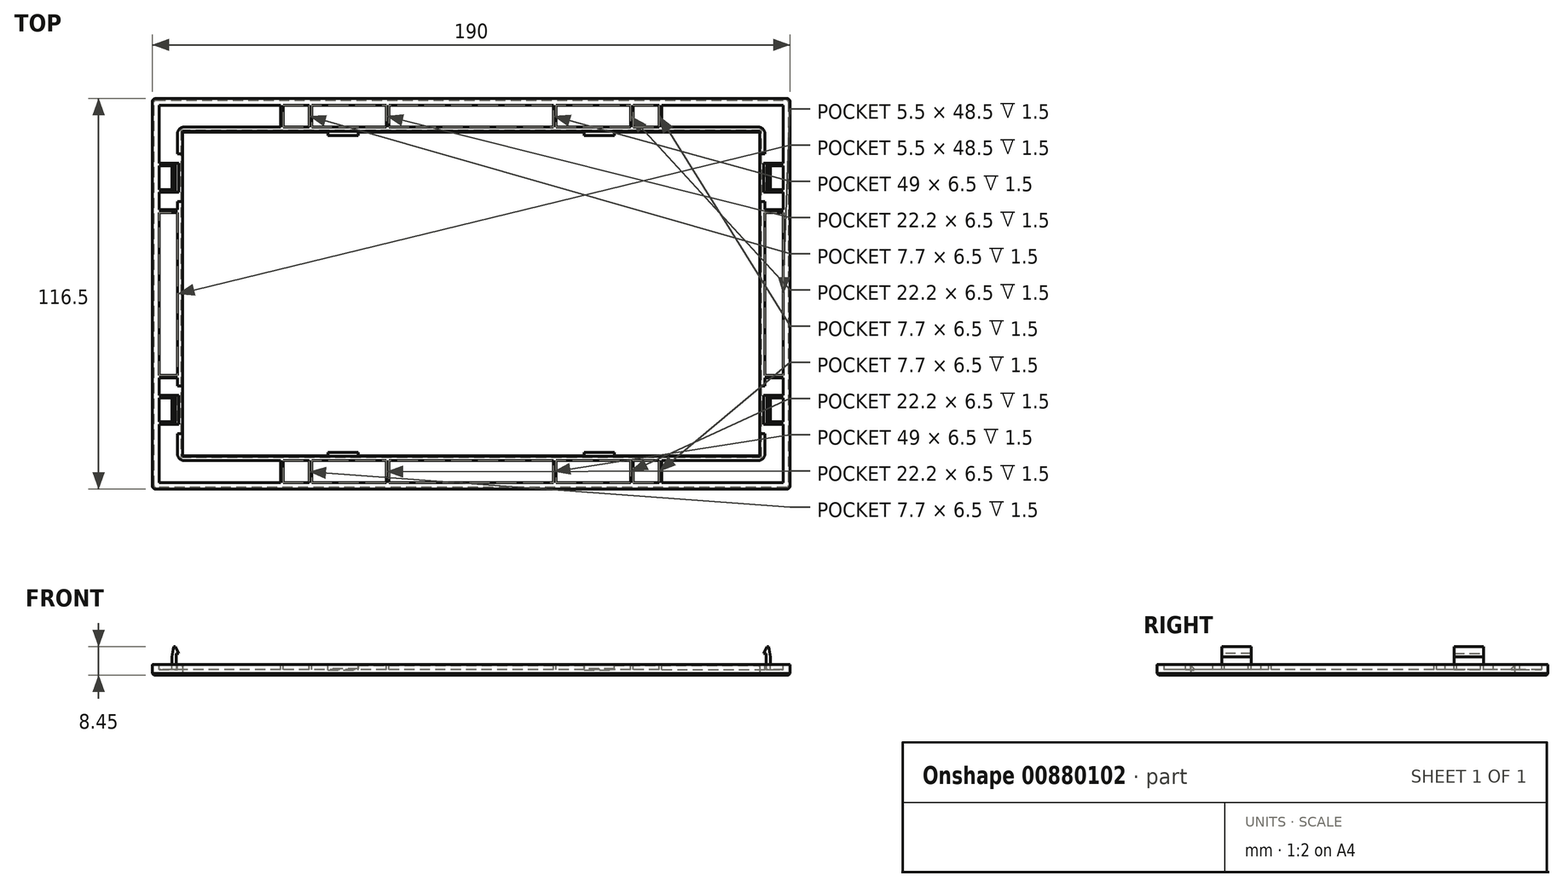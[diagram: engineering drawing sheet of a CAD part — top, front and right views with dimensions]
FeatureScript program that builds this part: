
annotation { "Feature Type Name" : "Feature", "Feature Type Description" : "" }
export const myFeature = defineFeature(function(context is Context, id is Id, definition is map)
    precondition{}
    {
        {
            var Q0;
            Q0=qCreatedBy(makeId("Top.planeOp"),FACE);
            var sketch = newSketch(context, id + "F0", { "sketchPlane" : qUnion([Q0])});
            skLineSegment(sketch, "E0", {"start": v(0, -58.25) * mm, "end": v(95, -58.25) * mm});
            skLineSegment(sketch, "E1", {"start": v(95, -58.25) * mm, "end": v(95, 0) * mm});
            skLineSegment(sketch, "E2", {"start": v(0, -48.25) * mm, "end": v(86, -48.25) * mm});
            skLineSegment(sketch, "E3", {"start": v(86, -48.25) * mm, "end": v(86, 0) * mm});
            skLineSegment(sketch, "E4.MirrorCS", {"start": v(95, 58.25) * mm, "end": v(95, 0) * mm});
            skLineSegment(sketch, "E5.MirrorCS", {"start": v(86, 48.25) * mm, "end": v(86, 0) * mm});
            skLineSegment(sketch, "E6.MirrorCS", {"start": v(0, 48.25) * mm, "end": v(86, 48.25) * mm});
            skLineSegment(sketch, "E7.MirrorCS", {"start": v(0, 58.25) * mm, "end": v(95, 58.25) * mm});
            skLineSegment(sketch, "E8.MirrorCS", {"start": v(0, 58.25) * mm, "end": v(-95, 58.25) * mm});
            skLineSegment(sketch, "E9.MirrorCS", {"start": v(0, 48.25) * mm, "end": v(-86, 48.25) * mm});
            skLineSegment(sketch, "E10.MirrorCS", {"start": v(-86, 48.25) * mm, "end": v(-86, 0) * mm});
            skLineSegment(sketch, "E11.MirrorCS", {"start": v(-95, 58.25) * mm, "end": v(-95, 0) * mm});
            skLineSegment(sketch, "E12.MirrorCS", {"start": v(-95, -58.25) * mm, "end": v(-95, 0) * mm});
            skLineSegment(sketch, "E13.MirrorCS", {"start": v(-86, -48.25) * mm, "end": v(-86, 0) * mm});
            skLineSegment(sketch, "E14.MirrorCS", {"start": v(0, -58.25) * mm, "end": v(-95, -58.25) * mm});
            skLineSegment(sketch, "E15.MirrorCS", {"start": v(0, -48.25) * mm, "end": v(-86, -48.25) * mm});
            skSolve(sketch);
        }
        {
            var Q0;
            Q0=makeQuery(id+"F0.imprint","IMPRINT",FACE,{"disambiguationData":[TD([[makeQuery(id+"F0.imprint","IMPRINT",EDGE,{"derivedFrom":sQuery(id+"F0.wireOp",EDGE,"E0")}),1.0]])]});
            extrude(context, id + "F1", {"entities" : qUnion([Q0]), "depth" : 1.65 * mm, "offsetDistance" : 25 * mm});
        }
        {
            var Q0;
            Q0=makeQuery(id+"F1.opExtrude","CAP_FACE",FACE,{"disambiguationData":[OSD([sQuery(id+"F0.wireOp",EDGE,"E0"),sQuery(id+"F0.wireOp",EDGE,"E1"),sQuery(id+"F0.wireOp",EDGE,"E2"),sQuery(id+"F0.wireOp",EDGE,"E3"),sQuery(id+"F0.wireOp",EDGE,"E4.MirrorCS"),sQuery(id+"F0.wireOp",EDGE,"E5.MirrorCS"),sQuery(id+"F0.wireOp",EDGE,"E6.MirrorCS"),sQuery(id+"F0.wireOp",EDGE,"E7.MirrorCS"),sQuery(id+"F0.wireOp",EDGE,"E8.MirrorCS"),sQuery(id+"F0.wireOp",EDGE,"E9.MirrorCS"),sQuery(id+"F0.wireOp",EDGE,"E10.MirrorCS"),sQuery(id+"F0.wireOp",EDGE,"E11.MirrorCS"),sQuery(id+"F0.wireOp",EDGE,"E12.MirrorCS"),sQuery(id+"F0.wireOp",EDGE,"E13.MirrorCS"),sQuery(id+"F0.wireOp",EDGE,"E14.MirrorCS"),sQuery(id+"F0.wireOp",EDGE,"E15.MirrorCS")])],"isStart":false});
            var sketch = newSketch(context, id + "F2", { "sketchPlane" : qUnion([Q0])});
            skLineSegment(sketch, "E16.0", {"start": v(0, 58.25) * mm, "end": v(-95, 58.25) * mm});
            skLineSegment(sketch, "E17.0", {"start": v(-95, 58.25) * mm, "end": v(-95, 0) * mm});
            skLineSegment(sketch, "E18.0", {"start": v(-95, -58.25) * mm, "end": v(-95, 0) * mm});
            skLineSegment(sketch, "E19.0", {"start": v(0, -58.25) * mm, "end": v(-95, -58.25) * mm});
            skLineSegment(sketch, "E20.0", {"start": v(0, -58.25) * mm, "end": v(95, -58.25) * mm});
            skLineSegment(sketch, "E21.0", {"start": v(95, -58.25) * mm, "end": v(95, 0) * mm});
            skLineSegment(sketch, "E22.0", {"start": v(95, 58.25) * mm, "end": v(95, 0) * mm});
            skLineSegment(sketch, "E23.0", {"start": v(0, 58.25) * mm, "end": v(95, 58.25) * mm});
            skLineSegment(sketch, "E24.0", {"start": v(0, 56.25) * mm, "end": v(93, 56.25) * mm});
            skLineSegment(sketch, "E24.1", {"start": v(93, 56.25) * mm, "end": v(93, 0) * mm});
            skLineSegment(sketch, "E24.2", {"start": v(0, 56.25) * mm, "end": v(-93, 56.25) * mm});
            skLineSegment(sketch, "E24.3", {"start": v(93, -56.25) * mm, "end": v(93, 0) * mm});
            skLineSegment(sketch, "E24.4", {"start": v(-93, 56.25) * mm, "end": v(-93, 0) * mm});
            skLineSegment(sketch, "E24.5", {"start": v(-93, -56.25) * mm, "end": v(-93, 0) * mm});
            skLineSegment(sketch, "E24.6", {"start": v(0, -56.25) * mm, "end": v(-93, -56.25) * mm});
            skLineSegment(sketch, "E24.7", {"start": v(0, -56.25) * mm, "end": v(93, -56.25) * mm});
            skSolve(sketch);
        }
        {
            var Q0;
            Q0 = qSketchRegion(id + "F2", true);
            extrude(context, id + "F3", {"entities" : qUnion([Q0]), "operationType" : NewBodyOperationType.ADD, "depth" : 1.5 * mm, "offsetDistance" : 25 * mm});
        }
        {
            var Q0;
            Q0=makeQuery(id+"F3.boolean.opBoolean","MERGE",EDGE,{"derivedFrom":[makeQuery(id+"F1.opExtrude","SWEPT_EDGE",EDGE,{"disambiguationData":[OSD([sQuery(id+"F0.wireOp",EDGE,"E12.MirrorCS"),sQuery(id+"F0.wireOp",EDGE,"E14.MirrorCS")])]}),makeQuery(id+"F3.opExtrude","SWEPT_EDGE",EDGE,{"disambiguationData":[OSD([sQuery(id+"F2.wireOp",EDGE,"E18.0"),sQuery(id+"F2.wireOp",EDGE,"E19.0")])]})]});
            var Q1;
            Q1=makeQuery(id+"F3.boolean.opBoolean","MERGE",EDGE,{"derivedFrom":[makeQuery(id+"F1.opExtrude","SWEPT_EDGE",EDGE,{"disambiguationData":[OSD([sQuery(id+"F0.wireOp",EDGE,"E0"),sQuery(id+"F0.wireOp",EDGE,"E1")])]}),makeQuery(id+"F3.opExtrude","SWEPT_EDGE",EDGE,{"disambiguationData":[OSD([sQuery(id+"F2.wireOp",EDGE,"E20.0"),sQuery(id+"F2.wireOp",EDGE,"E21.0")])]})]});
            var Q2;
            Q2=makeQuery(id+"F3.boolean.opBoolean","MERGE",EDGE,{"derivedFrom":[makeQuery(id+"F1.opExtrude","SWEPT_EDGE",EDGE,{"disambiguationData":[OSD([sQuery(id+"F0.wireOp",EDGE,"E4.MirrorCS"),sQuery(id+"F0.wireOp",EDGE,"E7.MirrorCS")])]}),makeQuery(id+"F3.opExtrude","SWEPT_EDGE",EDGE,{"disambiguationData":[OSD([sQuery(id+"F2.wireOp",EDGE,"E22.0"),sQuery(id+"F2.wireOp",EDGE,"E23.0")])]})]});
            var Q3;
            Q3=makeQuery(id+"F3.boolean.opBoolean","MERGE",EDGE,{"derivedFrom":[makeQuery(id+"F1.opExtrude","SWEPT_EDGE",EDGE,{"disambiguationData":[OSD([sQuery(id+"F0.wireOp",EDGE,"E8.MirrorCS"),sQuery(id+"F0.wireOp",EDGE,"E11.MirrorCS")])]}),makeQuery(id+"F3.opExtrude","SWEPT_EDGE",EDGE,{"disambiguationData":[OSD([sQuery(id+"F2.wireOp",EDGE,"E16.0"),sQuery(id+"F2.wireOp",EDGE,"E17.0")])]})]});
            fillet(context, id + "F4", {"entities" : qUnion([Q0, Q1, Q2, Q3]), "radius" : 1 * mm, "tangentPropagation" : true, "allowEdgeOverflow" : false});
        }
        {
            var Q0;
            Q0=makeQuery(id+"F1.opExtrude","CAP_EDGE",EDGE,{"disambiguationData":[OSD([sQuery(id+"F0.wireOp",EDGE,"E1"),sQuery(id+"F0.wireOp",EDGE,"E4.MirrorCS")])],"isStart":true});
            var Q1;
            Q1=makeQuery(id+"F1.opExtrude","CAP_EDGE",EDGE,{"disambiguationData":[OSD([sQuery(id+"F0.wireOp",EDGE,"E7.MirrorCS"),sQuery(id+"F0.wireOp",EDGE,"E8.MirrorCS")])],"isStart":true});
            var Q2;
            Q2=makeQuery(id+"F1.opExtrude","CAP_EDGE",EDGE,{"disambiguationData":[OSD([sQuery(id+"F0.wireOp",EDGE,"E11.MirrorCS"),sQuery(id+"F0.wireOp",EDGE,"E12.MirrorCS")])],"isStart":true});
            var Q3;
            Q3=makeQuery(id+"F1.opExtrude","CAP_EDGE",EDGE,{"disambiguationData":[OSD([sQuery(id+"F0.wireOp",EDGE,"E0"),sQuery(id+"F0.wireOp",EDGE,"E14.MirrorCS")])],"isStart":true});
            var Q4;
            Q4=makeQuery(id+"F1.opExtrude","CAP_EDGE",EDGE,{"disambiguationData":[OSD([sQuery(id+"F0.wireOp",EDGE,"E3"),sQuery(id+"F0.wireOp",EDGE,"E5.MirrorCS")])],"isStart":true});
            var Q5;
            Q5=makeQuery(id+"F1.opExtrude","CAP_EDGE",EDGE,{"disambiguationData":[OSD([sQuery(id+"F0.wireOp",EDGE,"E6.MirrorCS"),sQuery(id+"F0.wireOp",EDGE,"E9.MirrorCS")])],"isStart":true});
            var Q6;
            Q6=makeQuery(id+"F1.opExtrude","CAP_EDGE",EDGE,{"disambiguationData":[OSD([sQuery(id+"F0.wireOp",EDGE,"E10.MirrorCS"),sQuery(id+"F0.wireOp",EDGE,"E13.MirrorCS")])],"isStart":true});
            var Q7;
            Q7=makeQuery(id+"F1.opExtrude","CAP_EDGE",EDGE,{"disambiguationData":[OSD([sQuery(id+"F0.wireOp",EDGE,"E2"),sQuery(id+"F0.wireOp",EDGE,"E15.MirrorCS")])],"isStart":true});
            chamfer(context, id + "F5", {"entities" : qUnion([Q0, Q1, Q2, Q3, Q4, Q5, Q6, Q7]), "width" : .5 * mm, "tangentPropagation" : true});
        }
        {
            var Q0;
            Q0=makeQuery(id+"F1.opExtrude","CAP_FACE",FACE,{"disambiguationData":[OSD([sQuery(id+"F0.wireOp",EDGE,"E0"),sQuery(id+"F0.wireOp",EDGE,"E1"),sQuery(id+"F0.wireOp",EDGE,"E2"),sQuery(id+"F0.wireOp",EDGE,"E3"),sQuery(id+"F0.wireOp",EDGE,"E4.MirrorCS"),sQuery(id+"F0.wireOp",EDGE,"E5.MirrorCS"),sQuery(id+"F0.wireOp",EDGE,"E6.MirrorCS"),sQuery(id+"F0.wireOp",EDGE,"E7.MirrorCS"),sQuery(id+"F0.wireOp",EDGE,"E8.MirrorCS"),sQuery(id+"F0.wireOp",EDGE,"E9.MirrorCS"),sQuery(id+"F0.wireOp",EDGE,"E10.MirrorCS"),sQuery(id+"F0.wireOp",EDGE,"E11.MirrorCS"),sQuery(id+"F0.wireOp",EDGE,"E12.MirrorCS"),sQuery(id+"F0.wireOp",EDGE,"E13.MirrorCS"),sQuery(id+"F0.wireOp",EDGE,"E14.MirrorCS"),sQuery(id+"F0.wireOp",EDGE,"E15.MirrorCS")])],"isStart":false});
            var sketch = newSketch(context, id + "F6", { "sketchPlane" : qUnion([Q0])});
            skLineSegment(sketch, "E25.0", {"start": v(-86, -48.25) * mm, "end": v(-86, 48.25) * mm});
            skLineSegment(sketch, "E26.0", {"start": v(86, 48.25) * mm, "end": v(-86, 48.25) * mm});
            skLineSegment(sketch, "E27.0", {"start": v(-86, -48.25) * mm, "end": v(86, -48.25) * mm});
            skLineSegment(sketch, "E28.0", {"start": v(86, 48.25) * mm, "end": v(86, -48.25) * mm});
            skLineSegment(sketch, "E29.0", {"start": v(87.5, 49.75) * mm, "end": v(-87.5, 49.75) * mm});
            skLineSegment(sketch, "E29.1", {"start": v(87.5, 49.75) * mm, "end": v(87.5, -49.75) * mm});
            skLineSegment(sketch, "E29.2", {"start": v(-87.5, -49.75) * mm, "end": v(87.5, -49.75) * mm});
            skLineSegment(sketch, "E29.3", {"start": v(-87.5, -49.75) * mm, "end": v(-87.5, 49.75) * mm});
            skPoint(sketch, "E30", {"position": v(-86, -41.75) * mm});
            skLineSegment(sketch, "E31", {"start": v(-86, -41.75) * mm, "end": v(-87.5, -41.75) * mm});
            skPoint(sketch, "E32", {"position": v(-86, -27.45) * mm});
            skLineSegment(sketch, "E33", {"start": v(-86, -27.45) * mm, "end": v(-87.5, -27.45) * mm});
            skLineSegment(sketch, "E34.MirrorCS", {"start": v(-86, 27.45) * mm, "end": v(-87.5, 27.45) * mm});
            skLineSegment(sketch, "E35.MirrorCS", {"start": v(-86, 41.75) * mm, "end": v(-87.5, 41.75) * mm});
            skLineSegment(sketch, "E36.MirrorCS", {"start": v(86, 41.75) * mm, "end": v(87.5, 41.75) * mm});
            skLineSegment(sketch, "E37.MirrorCS", {"start": v(86, 27.45) * mm, "end": v(87.5, 27.45) * mm});
            skLineSegment(sketch, "E38.MirrorCS", {"start": v(86, -27.45) * mm, "end": v(87.5, -27.45) * mm});
            skLineSegment(sketch, "E39.MirrorCS", {"start": v(86, -41.75) * mm, "end": v(87.5, -41.75) * mm});
            skSolve(sketch);
        }
        {
            var Q0;
            {var subQ4=sQuery(id+"F6.wireOp",EDGE,"E26.0");Q0=makeQuery(id+"F6.imprint","IMPRINT",FACE,{"disambiguationData":[TD([[makeQuery(id+"F6.imprint","IMPRINT",EDGE,{"derivedFrom":subQ4}),-1.0]])]});}
            var Q1;
            {var subQ0=sQuery(id+"F6.wireOp",EDGE,"E33");Q1=makeQuery(id+"F6.imprint","IMPRINT",FACE,{"disambiguationData":[TD([[makeQuery(id+"F6.imprint","IMPRINT",EDGE,{"derivedFrom":subQ0}),-1.0]])]});}
            var Q2;
            {var subQ3=sQuery(id+"F6.wireOp",EDGE,"E27.0");Q2=makeQuery(id+"F6.imprint","IMPRINT",FACE,{"disambiguationData":[TD([[makeQuery(id+"F6.imprint","IMPRINT",EDGE,{"derivedFrom":subQ3}),-1.0]])]});}
            var Q3;
            {var subQ0=sQuery(id+"F6.wireOp",EDGE,"E37.MirrorCS");Q3=makeQuery(id+"F6.imprint","IMPRINT",FACE,{"disambiguationData":[TD([[makeQuery(id+"F6.imprint","IMPRINT",EDGE,{"derivedFrom":subQ0}),-1.0]])]});}
            extrude(context, id + "F7", {"entities" : qUnion([Q0, Q1, Q2, Q3]), "operationType" : NewBodyOperationType.ADD, "depth" : 1.5 * mm, "offsetDistance" : 25 * mm});
        }
        {
            var Q0;
            Q0=makeQuery(id+"F7.opExtrude","SWEPT_EDGE",EDGE,{"disambiguationData":[OSD([sQuery(id+"F6.wireOp",EDGE,"E29.0"),sQuery(id+"F6.wireOp",EDGE,"E29.3")])]});
            var Q1;
            Q1=makeQuery(id+"F7.opExtrude","SWEPT_EDGE",EDGE,{"disambiguationData":[OSD([sQuery(id+"F6.wireOp",EDGE,"E29.2"),sQuery(id+"F6.wireOp",EDGE,"E29.3")])]});
            var Q2;
            Q2=makeQuery(id+"F7.opExtrude","SWEPT_EDGE",EDGE,{"disambiguationData":[OSD([sQuery(id+"F6.wireOp",EDGE,"E29.1"),sQuery(id+"F6.wireOp",EDGE,"E29.2")])]});
            var Q3;
            Q3=makeQuery(id+"F7.opExtrude","SWEPT_EDGE",EDGE,{"disambiguationData":[OSD([sQuery(id+"F6.wireOp",EDGE,"E29.0"),sQuery(id+"F6.wireOp",EDGE,"E29.1")])]});
            fillet(context, id + "F8", {"entities" : qUnion([Q0, Q1, Q2, Q3]), "radius" : 2 * mm, "tangentPropagation" : true, "allowEdgeOverflow" : false});
        }
        {
            var Q0;
            Q0=makeQuery(id+"F7.boolean.opBoolean","MERGE",EDGE,{"derivedFrom":[makeQuery(id+"F1.opExtrude","SWEPT_EDGE",EDGE,{"disambiguationData":[OSD([sQuery(id+"F0.wireOp",EDGE,"E9.MirrorCS"),sQuery(id+"F0.wireOp",EDGE,"E10.MirrorCS")])]}),makeQuery(id+"F7.opExtrude","SWEPT_EDGE",EDGE,{"disambiguationData":[OSD([sQuery(id+"F6.wireOp",EDGE,"E25.0"),sQuery(id+"F6.wireOp",EDGE,"E26.0")])]})]});
            var Q1;
            Q1=makeQuery(id+"F7.boolean.opBoolean","MERGE",EDGE,{"derivedFrom":[makeQuery(id+"F1.opExtrude","SWEPT_EDGE",EDGE,{"disambiguationData":[OSD([sQuery(id+"F0.wireOp",EDGE,"E13.MirrorCS"),sQuery(id+"F0.wireOp",EDGE,"E15.MirrorCS")])]}),makeQuery(id+"F7.opExtrude","SWEPT_EDGE",EDGE,{"disambiguationData":[OSD([sQuery(id+"F6.wireOp",EDGE,"E25.0"),sQuery(id+"F6.wireOp",EDGE,"E27.0")])]})]});
            var Q2;
            Q2=makeQuery(id+"F7.boolean.opBoolean","MERGE",EDGE,{"derivedFrom":[makeQuery(id+"F1.opExtrude","SWEPT_EDGE",EDGE,{"disambiguationData":[OSD([sQuery(id+"F0.wireOp",EDGE,"E2"),sQuery(id+"F0.wireOp",EDGE,"E3")])]}),makeQuery(id+"F7.opExtrude","SWEPT_EDGE",EDGE,{"disambiguationData":[OSD([sQuery(id+"F6.wireOp",EDGE,"E27.0"),sQuery(id+"F6.wireOp",EDGE,"E28.0")])]})]});
            var Q3;
            Q3=makeQuery(id+"F7.boolean.opBoolean","MERGE",EDGE,{"derivedFrom":[makeQuery(id+"F1.opExtrude","SWEPT_EDGE",EDGE,{"disambiguationData":[OSD([sQuery(id+"F0.wireOp",EDGE,"E5.MirrorCS"),sQuery(id+"F0.wireOp",EDGE,"E6.MirrorCS")])]}),makeQuery(id+"F7.opExtrude","SWEPT_EDGE",EDGE,{"disambiguationData":[OSD([sQuery(id+"F6.wireOp",EDGE,"E26.0"),sQuery(id+"F6.wireOp",EDGE,"E28.0")])]})]});
            fillet(context, id + "F9", {"entities" : qUnion([Q0, Q1, Q2, Q3]), "radius" : .5 * mm, "tangentPropagation" : true, "allowEdgeOverflow" : false});
        }
        {
            var Q0;
            Q0=makeQuery(id+"F3.opExtrude","CAP_FACE",FACE,{"disambiguationData":[OSD([sQuery(id+"F2.wireOp",EDGE,"E16.0"),sQuery(id+"F2.wireOp",EDGE,"E17.0"),sQuery(id+"F2.wireOp",EDGE,"E18.0"),sQuery(id+"F2.wireOp",EDGE,"E19.0"),sQuery(id+"F2.wireOp",EDGE,"E20.0"),sQuery(id+"F2.wireOp",EDGE,"E21.0"),sQuery(id+"F2.wireOp",EDGE,"E22.0"),sQuery(id+"F2.wireOp",EDGE,"E23.0"),sQuery(id+"F2.wireOp",EDGE,"E24.0"),sQuery(id+"F2.wireOp",EDGE,"E24.1"),sQuery(id+"F2.wireOp",EDGE,"E24.2"),sQuery(id+"F2.wireOp",EDGE,"E24.3"),sQuery(id+"F2.wireOp",EDGE,"E24.4"),sQuery(id+"F2.wireOp",EDGE,"E24.5"),sQuery(id+"F2.wireOp",EDGE,"E24.6"),sQuery(id+"F2.wireOp",EDGE,"E24.7")])],"isStart":false});
            var sketch = newSketch(context, id + "F10", { "sketchPlane" : qUnion([Q0])});
            skLineSegment(sketch, "E40.0", {"start": v(-95, 57.25) * mm, "end": v(-95, -57.25) * mm, "construction": true});
            skLineSegment(sketch, "E41.0", {"start": v(-85.5, -49.75) * mm, "end": v(85.5, -49.75) * mm, "construction": true});
            skLineSegment(sketch, "E42.0", {"start": v(-93, -56.25) * mm, "end": v(93, -56.25) * mm, "construction": true});
            skPoint(sketch, "E43", {"position": v(-56, -56.25) * mm});
            skLineSegment(sketch, "E44.bottom", {"start": v(-56, -56.25) * mm, "end": v(-56.8, -56.25) * mm});
            skLineSegment(sketch, "E44.top", {"start": v(-56, -49.75) * mm, "end": v(-56.8, -49.75) * mm});
            skLineSegment(sketch, "E44.left", {"start": v(-56, -56.25) * mm, "end": v(-56, -49.75) * mm});
            skLineSegment(sketch, "E44.right", {"start": v(-56.8, -56.25) * mm, "end": v(-56.8, -49.75) * mm});
            skLineSegment(sketch, "E45.bottom", {"start": v(-47.5, -56.25) * mm, "end": v(-48.3, -56.25) * mm});
            skLineSegment(sketch, "E45.top", {"start": v(-47.5, -49.75) * mm, "end": v(-48.3, -49.75) * mm});
            skLineSegment(sketch, "E45.left", {"start": v(-47.5, -56.25) * mm, "end": v(-47.5, -49.75) * mm});
            skLineSegment(sketch, "E45.right", {"start": v(-48.3, -56.25) * mm, "end": v(-48.3, -49.75) * mm});
            skLineSegment(sketch, "E46.bottom", {"start": v(-24.5, -56.25) * mm, "end": v(-25.3, -56.25) * mm});
            skLineSegment(sketch, "E46.top", {"start": v(-24.5, -49.75) * mm, "end": v(-25.3, -49.75) * mm});
            skLineSegment(sketch, "E46.left", {"start": v(-24.5, -56.25) * mm, "end": v(-24.5, -49.75) * mm});
            skLineSegment(sketch, "E46.right", {"start": v(-25.3, -56.25) * mm, "end": v(-25.3, -49.75) * mm});
            skLineSegment(sketch, "E47.MirrorCS", {"start": v(56, -56.25) * mm, "end": v(56.8, -56.25) * mm});
            skLineSegment(sketch, "E48.MirrorCS", {"start": v(24.5, -56.25) * mm, "end": v(25.3, -56.25) * mm});
            skLineSegment(sketch, "E49.MirrorCS", {"start": v(56, -49.75) * mm, "end": v(56.8, -49.75) * mm});
            skLineSegment(sketch, "E50.MirrorCS", {"start": v(24.5, -49.75) * mm, "end": v(25.3, -49.75) * mm});
            skLineSegment(sketch, "E51.MirrorCS", {"start": v(47.5, -56.25) * mm, "end": v(48.3, -56.25) * mm});
            skLineSegment(sketch, "E52.MirrorCS", {"start": v(47.5, -49.75) * mm, "end": v(48.3, -49.75) * mm});
            skLineSegment(sketch, "E53.MirrorCS", {"start": v(56.8, -56.25) * mm, "end": v(56.8, -49.75) * mm});
            skLineSegment(sketch, "E54.MirrorCS", {"start": v(48.3, -56.25) * mm, "end": v(48.3, -49.75) * mm});
            skPoint(sketch, "E55.MirrorP", {"position": v(56, -56.25) * mm});
            skLineSegment(sketch, "E56.MirrorCS", {"start": v(24.5, -56.25) * mm, "end": v(24.5, -49.75) * mm});
            skLineSegment(sketch, "E57.MirrorCS", {"start": v(47.5, -56.25) * mm, "end": v(47.5, -49.75) * mm});
            skLineSegment(sketch, "E58.MirrorCS", {"start": v(56, -56.25) * mm, "end": v(56, -49.75) * mm});
            skLineSegment(sketch, "E59.MirrorCS", {"start": v(25.3, -56.25) * mm, "end": v(25.3, -49.75) * mm});
            skLineSegment(sketch, "E60.MirrorCS", {"start": v(-56, 56.25) * mm, "end": v(-56.8, 56.25) * mm});
            skLineSegment(sketch, "E61.MirrorCS", {"start": v(56, 56.25) * mm, "end": v(56.8, 56.25) * mm});
            skLineSegment(sketch, "E62.MirrorCS", {"start": v(47.5, 56.25) * mm, "end": v(48.3, 56.25) * mm});
            skLineSegment(sketch, "E63.MirrorCS", {"start": v(-47.5, 49.75) * mm, "end": v(-48.3, 49.75) * mm});
            skLineSegment(sketch, "E64.MirrorCS", {"start": v(47.5, 49.75) * mm, "end": v(48.3, 49.75) * mm});
            skLineSegment(sketch, "E65.MirrorCS", {"start": v(-47.5, 56.25) * mm, "end": v(-48.3, 56.25) * mm});
            skLineSegment(sketch, "E66.MirrorCS", {"start": v(56, 49.75) * mm, "end": v(56.8, 49.75) * mm});
            skLineSegment(sketch, "E67.MirrorCS", {"start": v(-24.5, 49.75) * mm, "end": v(-25.3, 49.75) * mm});
            skLineSegment(sketch, "E68.MirrorCS", {"start": v(-56, 49.75) * mm, "end": v(-56.8, 49.75) * mm});
            skLineSegment(sketch, "E69.MirrorCS", {"start": v(24.5, 49.75) * mm, "end": v(25.3, 49.75) * mm});
            skLineSegment(sketch, "E70.MirrorCS", {"start": v(-24.5, 56.25) * mm, "end": v(-25.3, 56.25) * mm});
            skLineSegment(sketch, "E71.MirrorCS", {"start": v(24.5, 56.25) * mm, "end": v(25.3, 56.25) * mm});
            skLineSegment(sketch, "E72.MirrorCS", {"start": v(56.8, 56.25) * mm, "end": v(56.8, 49.75) * mm});
            skLineSegment(sketch, "E73.MirrorCS", {"start": v(-56.8, 56.25) * mm, "end": v(-56.8, 49.75) * mm});
            skLineSegment(sketch, "E74.MirrorCS", {"start": v(-56, 56.25) * mm, "end": v(-56, 49.75) * mm});
            skPoint(sketch, "E75.MirrorP", {"position": v(-56, 56.25) * mm});
            skLineSegment(sketch, "E76.MirrorCS", {"start": v(-25.3, 56.25) * mm, "end": v(-25.3, 49.75) * mm});
            skLineSegment(sketch, "E77.MirrorCS", {"start": v(25.3, 56.25) * mm, "end": v(25.3, 49.75) * mm});
            skPoint(sketch, "E78.MirrorP", {"position": v(56, 56.25) * mm});
            skLineSegment(sketch, "E79.MirrorCS", {"start": v(47.5, 56.25) * mm, "end": v(47.5, 49.75) * mm});
            skLineSegment(sketch, "E80.MirrorCS", {"start": v(-48.3, 56.25) * mm, "end": v(-48.3, 49.75) * mm});
            skLineSegment(sketch, "E81.MirrorCS", {"start": v(-47.5, 56.25) * mm, "end": v(-47.5, 49.75) * mm});
            skLineSegment(sketch, "E82.MirrorCS", {"start": v(48.3, 56.25) * mm, "end": v(48.3, 49.75) * mm});
            skLineSegment(sketch, "E83.MirrorCS", {"start": v(-24.5, 56.25) * mm, "end": v(-24.5, 49.75) * mm});
            skLineSegment(sketch, "E84.MirrorCS", {"start": v(24.5, 56.25) * mm, "end": v(24.5, 49.75) * mm});
            skLineSegment(sketch, "E85.MirrorCS", {"start": v(56, 56.25) * mm, "end": v(56, 49.75) * mm});
            skSolve(sketch);
        }
        {
            var Q0;
            Q0=makeQuery(id+"F10.imprint","IMPRINT",FACE,{"disambiguationData":[TD([[makeQuery(id+"F10.imprint","IMPRINT",EDGE,{"derivedFrom":sQuery(id+"F10.wireOp",EDGE,"E44.bottom")}),1.0]])]});
            var Q1;
            Q1=makeQuery(id+"F10.imprint","IMPRINT",FACE,{"disambiguationData":[TD([[makeQuery(id+"F10.imprint","IMPRINT",EDGE,{"derivedFrom":sQuery(id+"F10.wireOp",EDGE,"E45.bottom")}),1.0]])]});
            var Q2;
            Q2=makeQuery(id+"F10.imprint","IMPRINT",FACE,{"disambiguationData":[TD([[makeQuery(id+"F10.imprint","IMPRINT",EDGE,{"derivedFrom":sQuery(id+"F10.wireOp",EDGE,"E46.bottom")}),1.0]])]});
            var Q3;
            Q3=makeQuery(id+"F10.imprint","IMPRINT",FACE,{"disambiguationData":[TD([[makeQuery(id+"F10.imprint","IMPRINT",EDGE,{"derivedFrom":sQuery(id+"F10.wireOp",EDGE,"E47.MirrorCS")}),1.0]])]});
            var Q4;
            Q4=makeQuery(id+"F10.imprint","IMPRINT",FACE,{"disambiguationData":[TD([[makeQuery(id+"F10.imprint","IMPRINT",EDGE,{"derivedFrom":sQuery(id+"F10.wireOp",EDGE,"E67.MirrorCS")}),-1.0]])]});
            var Q5;
            Q5=makeQuery(id+"F10.imprint","IMPRINT",FACE,{"disambiguationData":[TD([[makeQuery(id+"F10.imprint","IMPRINT",EDGE,{"derivedFrom":sQuery(id+"F10.wireOp",EDGE,"E69.MirrorCS")}),1.0]])]});
            var Q6;
            Q6=makeQuery(id+"F10.imprint","IMPRINT",FACE,{"disambiguationData":[TD([[makeQuery(id+"F10.imprint","IMPRINT",EDGE,{"derivedFrom":sQuery(id+"F10.wireOp",EDGE,"E63.MirrorCS")}),-1.0]])]});
            var Q7;
            Q7=makeQuery(id+"F10.imprint","IMPRINT",FACE,{"disambiguationData":[TD([[makeQuery(id+"F10.imprint","IMPRINT",EDGE,{"derivedFrom":sQuery(id+"F10.wireOp",EDGE,"E62.MirrorCS")}),1.0]])]});
            var Q8;
            Q8=makeQuery(id+"F10.imprint","IMPRINT",FACE,{"disambiguationData":[TD([[makeQuery(id+"F10.imprint","IMPRINT",EDGE,{"derivedFrom":sQuery(id+"F10.wireOp",EDGE,"E61.MirrorCS")}),1.0]])]});
            var Q9;
            Q9=makeQuery(id+"F10.imprint","IMPRINT",FACE,{"disambiguationData":[TD([[makeQuery(id+"F10.imprint","IMPRINT",EDGE,{"derivedFrom":sQuery(id+"F10.wireOp",EDGE,"E60.MirrorCS")}),1.0]])]});
            var Q10;
            Q10=makeQuery(id+"F10.imprint","IMPRINT",FACE,{"disambiguationData":[TD([[makeQuery(id+"F10.imprint","IMPRINT",EDGE,{"derivedFrom":sQuery(id+"F10.wireOp",EDGE,"E51.MirrorCS")}),1.0]])]});
            var Q11;
            Q11=makeQuery(id+"F10.imprint","IMPRINT",FACE,{"disambiguationData":[TD([[makeQuery(id+"F10.imprint","IMPRINT",EDGE,{"derivedFrom":sQuery(id+"F10.wireOp",EDGE,"E48.MirrorCS")}),1.0]])]});
            extrude(context, id + "F11", {"entities" : qUnion([Q0, Q1, Q2, Q3, Q4, Q5, Q6, Q7, Q8, Q9, Q10, Q11]), "operationType" : NewBodyOperationType.ADD, "endBound" : BoundingType.UP_TO_NEXT, "oppositeDirection" : true, "depth" : 25 * mm, "offsetDistance" : 25 * mm});
        }
        {
            var Q0;
            {var subQ0=sQuery(id+"F6.wireOp",EDGE,"E29.3");var subQ1=sQuery(id+"F6.wireOp",EDGE,"E29.1");var subQ2=sQuery(id+"F6.wireOp",EDGE,"E28.0");var subQ3=sQuery(id+"F6.wireOp",EDGE,"E25.0");Q0=makeQuery(id+"F11.boolean.opBoolean","MERGE",FACE,{"derivedFrom":[makeQuery(id+"F3.opExtrude","CAP_FACE",FACE,{"disambiguationData":[OSD([sQuery(id+"F2.wireOp",EDGE,"E16.0"),sQuery(id+"F2.wireOp",EDGE,"E17.0"),sQuery(id+"F2.wireOp",EDGE,"E18.0"),sQuery(id+"F2.wireOp",EDGE,"E19.0"),sQuery(id+"F2.wireOp",EDGE,"E20.0"),sQuery(id+"F2.wireOp",EDGE,"E21.0"),sQuery(id+"F2.wireOp",EDGE,"E22.0"),sQuery(id+"F2.wireOp",EDGE,"E23.0"),sQuery(id+"F2.wireOp",EDGE,"E24.0"),sQuery(id+"F2.wireOp",EDGE,"E24.1"),sQuery(id+"F2.wireOp",EDGE,"E24.2"),sQuery(id+"F2.wireOp",EDGE,"E24.3"),sQuery(id+"F2.wireOp",EDGE,"E24.4"),sQuery(id+"F2.wireOp",EDGE,"E24.5"),sQuery(id+"F2.wireOp",EDGE,"E24.6"),sQuery(id+"F2.wireOp",EDGE,"E24.7")])],"isStart":false}),makeQuery(id+"F7.opExtrude","CAP_FACE",FACE,{"disambiguationData":[OSD([subQ3,sQuery(id+"F6.wireOp",EDGE,"E27.0"),subQ2,subQ1,sQuery(id+"F6.wireOp",EDGE,"E29.2"),subQ0,sQuery(id+"F6.wireOp",EDGE,"E31"),sQuery(id+"F6.wireOp",EDGE,"E39.MirrorCS")])],"isStart":false}),makeQuery(id+"F7.opExtrude","CAP_FACE",FACE,{"disambiguationData":[OSD([subQ3,sQuery(id+"F6.wireOp",EDGE,"E26.0"),subQ2,sQuery(id+"F6.wireOp",EDGE,"E29.0"),subQ1,subQ0,sQuery(id+"F6.wireOp",EDGE,"E35.MirrorCS"),sQuery(id+"F6.wireOp",EDGE,"E36.MirrorCS")])],"isStart":false}),makeQuery(id+"F11.opExtrude","CAP_FACE",FACE,{"disambiguationData":[OSD([sQuery(id+"F10.wireOp",EDGE,"E44.bottom"),sQuery(id+"F10.wireOp",EDGE,"E44.top"),sQuery(id+"F10.wireOp",EDGE,"E44.left"),sQuery(id+"F10.wireOp",EDGE,"E44.right")])],"isStart":true}),makeQuery(id+"F11.opExtrude","CAP_FACE",FACE,{"disambiguationData":[OSD([sQuery(id+"F10.wireOp",EDGE,"E45.bottom"),sQuery(id+"F10.wireOp",EDGE,"E45.top"),sQuery(id+"F10.wireOp",EDGE,"E45.left"),sQuery(id+"F10.wireOp",EDGE,"E45.right")])],"isStart":true}),makeQuery(id+"F11.opExtrude","CAP_FACE",FACE,{"disambiguationData":[OSD([sQuery(id+"F10.wireOp",EDGE,"E46.bottom"),sQuery(id+"F10.wireOp",EDGE,"E46.top"),sQuery(id+"F10.wireOp",EDGE,"E46.left"),sQuery(id+"F10.wireOp",EDGE,"E46.right")])],"isStart":true}),makeQuery(id+"F11.opExtrude","CAP_FACE",FACE,{"disambiguationData":[OSD([sQuery(id+"F10.wireOp",EDGE,"E47.MirrorCS"),sQuery(id+"F10.wireOp",EDGE,"E49.MirrorCS"),sQuery(id+"F10.wireOp",EDGE,"E53.MirrorCS"),sQuery(id+"F10.wireOp",EDGE,"E58.MirrorCS")])],"isStart":true}),makeQuery(id+"F11.opExtrude","CAP_FACE",FACE,{"disambiguationData":[OSD([sQuery(id+"F10.wireOp",EDGE,"E48.MirrorCS"),sQuery(id+"F10.wireOp",EDGE,"E50.MirrorCS"),sQuery(id+"F10.wireOp",EDGE,"E56.MirrorCS"),sQuery(id+"F10.wireOp",EDGE,"E59.MirrorCS")])],"isStart":true}),makeQuery(id+"F11.opExtrude","CAP_FACE",FACE,{"disambiguationData":[OSD([sQuery(id+"F10.wireOp",EDGE,"E51.MirrorCS"),sQuery(id+"F10.wireOp",EDGE,"E52.MirrorCS"),sQuery(id+"F10.wireOp",EDGE,"E54.MirrorCS"),sQuery(id+"F10.wireOp",EDGE,"E57.MirrorCS")])],"isStart":true}),makeQuery(id+"F11.opExtrude","CAP_FACE",FACE,{"disambiguationData":[OSD([sQuery(id+"F10.wireOp",EDGE,"E60.MirrorCS"),sQuery(id+"F10.wireOp",EDGE,"E68.MirrorCS"),sQuery(id+"F10.wireOp",EDGE,"E73.MirrorCS"),sQuery(id+"F10.wireOp",EDGE,"E74.MirrorCS")])],"isStart":true}),makeQuery(id+"F11.opExtrude","CAP_FACE",FACE,{"disambiguationData":[OSD([sQuery(id+"F10.wireOp",EDGE,"E61.MirrorCS"),sQuery(id+"F10.wireOp",EDGE,"E66.MirrorCS"),sQuery(id+"F10.wireOp",EDGE,"E72.MirrorCS"),sQuery(id+"F10.wireOp",EDGE,"E85.MirrorCS")])],"isStart":true}),makeQuery(id+"F11.opExtrude","CAP_FACE",FACE,{"disambiguationData":[OSD([sQuery(id+"F10.wireOp",EDGE,"E62.MirrorCS"),sQuery(id+"F10.wireOp",EDGE,"E64.MirrorCS"),sQuery(id+"F10.wireOp",EDGE,"E79.MirrorCS"),sQuery(id+"F10.wireOp",EDGE,"E82.MirrorCS")])],"isStart":true}),makeQuery(id+"F11.opExtrude","CAP_FACE",FACE,{"disambiguationData":[OSD([sQuery(id+"F10.wireOp",EDGE,"E63.MirrorCS"),sQuery(id+"F10.wireOp",EDGE,"E65.MirrorCS"),sQuery(id+"F10.wireOp",EDGE,"E80.MirrorCS"),sQuery(id+"F10.wireOp",EDGE,"E81.MirrorCS")])],"isStart":true}),makeQuery(id+"F11.opExtrude","CAP_FACE",FACE,{"disambiguationData":[OSD([sQuery(id+"F10.wireOp",EDGE,"E67.MirrorCS"),sQuery(id+"F10.wireOp",EDGE,"E70.MirrorCS"),sQuery(id+"F10.wireOp",EDGE,"E76.MirrorCS"),sQuery(id+"F10.wireOp",EDGE,"E83.MirrorCS")])],"isStart":true}),makeQuery(id+"F11.opExtrude","CAP_FACE",FACE,{"disambiguationData":[OSD([sQuery(id+"F10.wireOp",EDGE,"E69.MirrorCS"),sQuery(id+"F10.wireOp",EDGE,"E71.MirrorCS"),sQuery(id+"F10.wireOp",EDGE,"E77.MirrorCS"),sQuery(id+"F10.wireOp",EDGE,"E84.MirrorCS")])],"isStart":true})]});}
            var sketch = newSketch(context, id + "F12", { "sketchPlane" : qUnion([Q0])});
            skLineSegment(sketch, "E86.0", {"start": v(85.5, 48.25) * mm, "end": v(-85.5, 48.25) * mm, "construction": true});
            skLineSegment(sketch, "E87.0", {"start": v(-95, 57.25) * mm, "end": v(-95, -57.25) * mm, "construction": true});
            skLineSegment(sketch, "E88.bottom", {"start": v(-33.65, 48.25) * mm, "end": v(-42.65, 48.25) * mm});
            skLineSegment(sketch, "E88.top", {"start": v(-33.65, 47.25) * mm, "end": v(-42.65, 47.25) * mm});
            skLineSegment(sketch, "E88.left", {"start": v(-33.65, 48.25) * mm, "end": v(-33.65, 47.25) * mm});
            skLineSegment(sketch, "E88.right", {"start": v(-42.65, 48.25) * mm, "end": v(-42.65, 47.25) * mm});
            skLineSegment(sketch, "E89.MirrorCS", {"start": v(33.65, 48.25) * mm, "end": v(33.65, 47.25) * mm});
            skLineSegment(sketch, "E90.MirrorCS", {"start": v(42.65, 48.25) * mm, "end": v(42.65, 47.25) * mm});
            skLineSegment(sketch, "E91.MirrorCS", {"start": v(33.65, 48.25) * mm, "end": v(42.65, 48.25) * mm});
            skLineSegment(sketch, "E92.MirrorCS", {"start": v(33.65, 47.25) * mm, "end": v(42.65, 47.25) * mm});
            skLineSegment(sketch, "E93.MirrorCS", {"start": v(-42.65, -48.25) * mm, "end": v(-42.65, -47.25) * mm});
            skLineSegment(sketch, "E94.MirrorCS", {"start": v(33.65, -48.25) * mm, "end": v(33.65, -47.25) * mm});
            skLineSegment(sketch, "E95.MirrorCS", {"start": v(-33.65, -48.25) * mm, "end": v(-33.65, -47.25) * mm});
            skLineSegment(sketch, "E96.MirrorCS", {"start": v(42.65, -48.25) * mm, "end": v(42.65, -47.25) * mm});
            skLineSegment(sketch, "E97.MirrorCS", {"start": v(33.65, -47.25) * mm, "end": v(42.65, -47.25) * mm});
            skLineSegment(sketch, "E98.MirrorCS", {"start": v(-33.65, -48.25) * mm, "end": v(-42.65, -48.25) * mm});
            skLineSegment(sketch, "E99.MirrorCS", {"start": v(-33.65, -47.25) * mm, "end": v(-42.65, -47.25) * mm});
            skLineSegment(sketch, "E100.MirrorCS", {"start": v(33.65, -48.25) * mm, "end": v(42.65, -48.25) * mm});
            skSolve(sketch);
        }
        {
            var Q0;
            Q0=makeQuery(id+"F12.imprint","IMPRINT",FACE,{"disambiguationData":[TD([[makeQuery(id+"F12.imprint","IMPRINT",EDGE,{"derivedFrom":sQuery(id+"F12.wireOp",EDGE,"E88.bottom")}),1.0]])]});
            var Q1;
            Q1=makeQuery(id+"F12.imprint","IMPRINT",FACE,{"disambiguationData":[TD([[makeQuery(id+"F12.imprint","IMPRINT",EDGE,{"derivedFrom":sQuery(id+"F12.wireOp",EDGE,"E89.MirrorCS")}),1.0]])]});
            var Q2;
            Q2=makeQuery(id+"F12.imprint","IMPRINT",FACE,{"disambiguationData":[TD([[makeQuery(id+"F12.imprint","IMPRINT",EDGE,{"derivedFrom":sQuery(id+"F12.wireOp",EDGE,"E94.MirrorCS")}),-1.0]])]});
            var Q3;
            Q3=makeQuery(id+"F12.imprint","IMPRINT",FACE,{"disambiguationData":[TD([[makeQuery(id+"F12.imprint","IMPRINT",EDGE,{"derivedFrom":sQuery(id+"F12.wireOp",EDGE,"E93.MirrorCS")}),-1.0]])]});
            extrude(context, id + "F13", {"entities" : qUnion([Q0, Q1, Q2, Q3]), "operationType" : NewBodyOperationType.ADD, "oppositeDirection" : true, "depth" : 1.7 * mm, "offsetDistance" : 25 * mm});
        }
        {
            var Q0;
            Q0=makeQuery(id+"F13.opExtrude","CAP_EDGE",EDGE,{"disambiguationData":[OSD([sQuery(id+"F12.wireOp",EDGE,"E99.MirrorCS")])],"isStart":true});
            var Q1;
            Q1=makeQuery(id+"F13.opExtrude","CAP_EDGE",EDGE,{"disambiguationData":[OSD([sQuery(id+"F12.wireOp",EDGE,"E97.MirrorCS")])],"isStart":true});
            var Q2;
            Q2=makeQuery(id+"F13.opExtrude","CAP_EDGE",EDGE,{"disambiguationData":[OSD([sQuery(id+"F12.wireOp",EDGE,"E88.top")])],"isStart":true});
            var Q3;
            Q3=makeQuery(id+"F13.opExtrude","CAP_EDGE",EDGE,{"disambiguationData":[OSD([sQuery(id+"F12.wireOp",EDGE,"E92.MirrorCS")])],"isStart":true});
            chamfer(context, id + "F14", {"entities" : qUnion([Q0, Q1, Q2, Q3]), "width" : 1.25 * mm, "tangentPropagation" : true});
        }
        {
            var Q0;
            {var subQ2=sQuery(id+"F6.wireOp",EDGE,"E31");var subQ8=sQuery(id+"F0.wireOp",EDGE,"E13.MirrorCS");var subQ9=sQuery(id+"F0.wireOp",EDGE,"E10.MirrorCS");Q0=makeQuery(id+"F11.boolean.opBoolean","SPLIT",FACE,{"disambiguationData":[TD([makeQuery(id+"F7.opExtrude","SWEPT_FACE",FACE,{"disambiguationData":[OSD([subQ2])]})])],"derivedFrom":makeQuery(id+"F1.opExtrude","CAP_FACE",FACE,{"disambiguationData":[OSD([sQuery(id+"F0.wireOp",EDGE,"E0"),sQuery(id+"F0.wireOp",EDGE,"E1"),sQuery(id+"F0.wireOp",EDGE,"E2"),sQuery(id+"F0.wireOp",EDGE,"E3"),sQuery(id+"F0.wireOp",EDGE,"E4.MirrorCS"),sQuery(id+"F0.wireOp",EDGE,"E5.MirrorCS"),sQuery(id+"F0.wireOp",EDGE,"E6.MirrorCS"),sQuery(id+"F0.wireOp",EDGE,"E7.MirrorCS"),sQuery(id+"F0.wireOp",EDGE,"E8.MirrorCS"),sQuery(id+"F0.wireOp",EDGE,"E9.MirrorCS"),subQ9,sQuery(id+"F0.wireOp",EDGE,"E11.MirrorCS"),sQuery(id+"F0.wireOp",EDGE,"E12.MirrorCS"),subQ8,sQuery(id+"F0.wireOp",EDGE,"E14.MirrorCS"),sQuery(id+"F0.wireOp",EDGE,"E15.MirrorCS")])],"isStart":false})});}
            var sketch = newSketch(context, id + "F15", { "sketchPlane" : qUnion([Q0])});
            skLineSegment(sketch, "E101.0", {"start": v(-87.5, -49.75) * mm, "end": v(-87.5, 49.75) * mm, "construction": true});
            skLineSegment(sketch, "E102.0", {"start": v(0, -58.25) * mm, "end": v(-95, -58.25) * mm, "construction": true});
            skPoint(sketch, "E103.0", {"position": v(-87.5, -27.45) * mm});
            skPoint(sketch, "E104.0", {"position": v(-87.5, -41.75) * mm});
            skLineSegment(sketch, "E105.bottom", {"start": v(-87.9, -30.25) * mm, "end": v(-89.1, -30.25) * mm});
            skLineSegment(sketch, "E105.top", {"start": v(-87.9, -38.95) * mm, "end": v(-89.1, -38.95) * mm});
            skLineSegment(sketch, "E105.left", {"start": v(-87.9, -30.25) * mm, "end": v(-87.9, -38.95) * mm});
            skLineSegment(sketch, "E105.right", {"start": v(-89.1, -30.25) * mm, "end": v(-89.1, -38.95) * mm});
            skLineSegment(sketch, "E106.MirrorCS", {"start": v(-87.9, 30.25) * mm, "end": v(-89.1, 30.25) * mm});
            skLineSegment(sketch, "E107.MirrorCS", {"start": v(-89.1, 30.25) * mm, "end": v(-89.1, 38.95) * mm});
            skLineSegment(sketch, "E108.MirrorCS", {"start": v(-87.9, 38.95) * mm, "end": v(-89.1, 38.95) * mm});
            skLineSegment(sketch, "E109.MirrorCS", {"start": v(-87.9, 30.25) * mm, "end": v(-87.9, 38.95) * mm});
            skLineSegment(sketch, "E110.MirrorCS", {"start": v(87.9, -38.95) * mm, "end": v(89.1, -38.95) * mm});
            skLineSegment(sketch, "E111.MirrorCS", {"start": v(87.9, 30.25) * mm, "end": v(89.1, 30.25) * mm});
            skLineSegment(sketch, "E112.MirrorCS", {"start": v(87.9, 38.95) * mm, "end": v(89.1, 38.95) * mm});
            skLineSegment(sketch, "E113.MirrorCS", {"start": v(87.9, -30.25) * mm, "end": v(89.1, -30.25) * mm});
            skLineSegment(sketch, "E114.MirrorCS", {"start": v(89.1, -30.25) * mm, "end": v(89.1, -38.95) * mm});
            skLineSegment(sketch, "E115.MirrorCS", {"start": v(87.9, -30.25) * mm, "end": v(87.9, -38.95) * mm});
            skLineSegment(sketch, "E116.MirrorCS", {"start": v(89.1, 30.25) * mm, "end": v(89.1, 38.95) * mm});
            skLineSegment(sketch, "E117.MirrorCS", {"start": v(87.9, 30.25) * mm, "end": v(87.9, 38.95) * mm});
            skSolve(sketch);
        }
        {
            var Q0;
            Q0=makeQuery(id+"F15.imprint","IMPRINT",FACE,{"disambiguationData":[TD([[makeQuery(id+"F15.imprint","IMPRINT",EDGE,{"derivedFrom":sQuery(id+"F15.wireOp",EDGE,"E105.bottom")}),1.0]])]});
            var Q1;
            Q1=makeQuery(id+"F15.imprint","IMPRINT",FACE,{"disambiguationData":[TD([[makeQuery(id+"F15.imprint","IMPRINT",EDGE,{"derivedFrom":sQuery(id+"F15.wireOp",EDGE,"E106.MirrorCS")}),-1.0]])]});
            var Q2;
            Q2=makeQuery(id+"F15.imprint","IMPRINT",FACE,{"disambiguationData":[TD([[makeQuery(id+"F15.imprint","IMPRINT",EDGE,{"derivedFrom":sQuery(id+"F15.wireOp",EDGE,"E111.MirrorCS")}),1.0]])]});
            var Q3;
            Q3=makeQuery(id+"F15.imprint","IMPRINT",FACE,{"disambiguationData":[TD([[makeQuery(id+"F15.imprint","IMPRINT",EDGE,{"derivedFrom":sQuery(id+"F15.wireOp",EDGE,"E110.MirrorCS")}),1.0]])]});
            extrude(context, id + "F16", {"entities" : qUnion([Q0, Q1, Q2, Q3]), "operationType" : NewBodyOperationType.ADD, "depth" : 6.8 * mm, "offsetDistance" : 25 * mm});
        }
        {
            var Q0;
            Q0=makeQuery(id+"F16.opExtrude","SWEPT_FACE",FACE,{"disambiguationData":[OSD([sQuery(id+"F15.wireOp",EDGE,"E105.left")])]});
            var sketch = newSketch(context, id + "F17", { "sketchPlane" : qUnion([Q0])});
            skLineSegment(sketch, "E118.0", {"start": v(-38.95, 8.45) * mm, "end": v(-38.95, 1.65) * mm, "construction": true});
            skLineSegment(sketch, "E119.0", {"start": v(-30.25, 8.45) * mm, "end": v(-38.95, 8.45) * mm, "construction": true});
            skLineSegment(sketch, "E120.0", {"start": v(-30.25, 8.45) * mm, "end": v(-30.25, 1.65) * mm, "construction": true});
            skLineSegment(sketch, "E121.bottom", {"start": v(-38.95, 8.45) * mm, "end": v(-30.25, 8.45) * mm});
            skLineSegment(sketch, "E121.top", {"start": v(-38.95, 6.45) * mm, "end": v(-30.25, 6.45) * mm});
            skLineSegment(sketch, "E121.left", {"start": v(-38.95, 8.45) * mm, "end": v(-38.95, 6.45) * mm});
            skLineSegment(sketch, "E121.right", {"start": v(-30.25, 8.45) * mm, "end": v(-30.25, 6.45) * mm});
            skLineSegment(sketch, "E122.MirrorCS", {"start": v(38.95, 8.45) * mm, "end": v(30.25, 8.45) * mm});
            skLineSegment(sketch, "E123.MirrorCS", {"start": v(30.25, 8.45) * mm, "end": v(30.25, 6.45) * mm});
            skLineSegment(sketch, "E124.MirrorCS", {"start": v(38.95, 6.45) * mm, "end": v(30.25, 6.45) * mm});
            skLineSegment(sketch, "E125.MirrorCS", {"start": v(38.95, 8.45) * mm, "end": v(38.95, 6.45) * mm});
            skLineSegment(sketch, "E126.MirrorCS", {"start": v(30.25, 8.45) * mm, "end": v(38.95, 8.45) * mm, "construction": true});
            skSolve(sketch);
        }
        {
            var Q0;
            Q0=makeQuery(id+"F17.imprint","IMPRINT",FACE,{"disambiguationData":[TD([[makeQuery(id+"F17.imprint","IMPRINT",EDGE,{"derivedFrom":sQuery(id+"F17.wireOp",EDGE,"E121.bottom")}),1.0]])]});
            var Q1;
            Q1=makeQuery(id+"F17.imprint","IMPRINT",FACE,{"disambiguationData":[TD([[makeQuery(id+"F17.imprint","IMPRINT",EDGE,{"derivedFrom":sQuery(id+"F17.wireOp",EDGE,"E122.MirrorCS")}),1.0]])]});
            extrude(context, id + "F18", {"entities" : qUnion([Q0, Q1]), "operationType" : NewBodyOperationType.ADD, "depth" : .8 * mm, "offsetDistance" : 25 * mm});
        }
        {
            var Q0;
            Q0=makeQuery(id+"F16.opExtrude","SWEPT_FACE",FACE,{"disambiguationData":[OSD([sQuery(id+"F15.wireOp",EDGE,"E115.MirrorCS")])]});
            var sketch = newSketch(context, id + "F19", { "sketchPlane" : qUnion([Q0])});
            skLineSegment(sketch, "E127.0", {"start": v(30.25, 8.45) * mm, "end": v(30.25, 1.65) * mm, "construction": true});
            skLineSegment(sketch, "E128.0", {"start": v(30.25, 8.45) * mm, "end": v(38.95, 8.45) * mm, "construction": true});
            skLineSegment(sketch, "E129.0", {"start": v(38.95, 8.45) * mm, "end": v(38.95, 1.65) * mm, "construction": true});
            skLineSegment(sketch, "E130.bottom", {"start": v(30.25, 8.45) * mm, "end": v(38.95, 8.45) * mm});
            skLineSegment(sketch, "E130.top", {"start": v(30.25, 6.45) * mm, "end": v(38.95, 6.45) * mm});
            skLineSegment(sketch, "E130.left", {"start": v(30.25, 8.45) * mm, "end": v(30.25, 6.45) * mm});
            skLineSegment(sketch, "E130.right", {"start": v(38.95, 8.45) * mm, "end": v(38.95, 6.45) * mm});
            skLineSegment(sketch, "E131.MirrorCS", {"start": v(-30.25, 8.45) * mm, "end": v(-38.95, 8.45) * mm});
            skLineSegment(sketch, "E132.MirrorCS", {"start": v(-30.25, 8.45) * mm, "end": v(-30.25, 6.45) * mm});
            skLineSegment(sketch, "E133.MirrorCS", {"start": v(-30.25, 6.45) * mm, "end": v(-38.95, 6.45) * mm});
            skLineSegment(sketch, "E134.MirrorCS", {"start": v(-38.95, 8.45) * mm, "end": v(-38.95, 6.45) * mm});
            skLineSegment(sketch, "E135.MirrorCS", {"start": v(-30.25, 8.45) * mm, "end": v(-38.95, 8.45) * mm, "construction": true});
            skSolve(sketch);
        }
        {
            var Q0;
            Q0=makeQuery(id+"F19.imprint","IMPRINT",FACE,{"disambiguationData":[TD([[makeQuery(id+"F19.imprint","IMPRINT",EDGE,{"derivedFrom":sQuery(id+"F19.wireOp",EDGE,"E131.MirrorCS")}),1.0]])]});
            var Q1;
            Q1=makeQuery(id+"F19.imprint","IMPRINT",FACE,{"disambiguationData":[TD([[makeQuery(id+"F19.imprint","IMPRINT",EDGE,{"derivedFrom":sQuery(id+"F19.wireOp",EDGE,"E130.bottom")}),-1.0]])]});
            extrude(context, id + "F20", {"entities" : qUnion([Q0, Q1]), "operationType" : NewBodyOperationType.ADD, "depth" : .8 * mm, "offsetDistance" : 25 * mm});
        }
        {
            var Q0;
            Q0=makeQuery(id+"F20.opExtrude","CAP_EDGE",EDGE,{"disambiguationData":[OSD([sQuery(id+"F19.wireOp",EDGE,"E131.MirrorCS")])],"isStart":false});
            var Q1;
            Q1=makeQuery(id+"F18.opExtrude","CAP_EDGE",EDGE,{"disambiguationData":[OSD([sQuery(id+"F17.wireOp",EDGE,"E122.MirrorCS")])],"isStart":false});
            var Q2;
            Q2=makeQuery(id+"F18.opExtrude","CAP_EDGE",EDGE,{"disambiguationData":[OSD([sQuery(id+"F17.wireOp",EDGE,"E121.bottom")])],"isStart":false});
            chamfer(context, id + "F21", {"entities" : qUnion([Q0, Q1, Q2]), "chamferType" : ChamferType.TWO_OFFSETS, "width1" : 2 * mm, "oppositeDirection" : false, "width2" : 1 * mm, "tangentPropagation" : true});
        }
        {
            var Q0;
            Q0=makeQuery(id+"F20.opExtrude","CAP_EDGE",EDGE,{"disambiguationData":[OSD([sQuery(id+"F19.wireOp",EDGE,"E130.bottom")])],"isStart":false});
            chamfer(context, id + "F22", {"entities" : qUnion([Q0]), "chamferType" : ChamferType.TWO_OFFSETS, "width1" : 1 * mm, "oppositeDirection" : false, "width2" : 2 * mm, "tangentPropagation" : true});
        }
        {
            var Q0;
            Q0=makeQuery(id+"F16.opExtrude","CAP_EDGE",EDGE,{"disambiguationData":[OSD([sQuery(id+"F15.wireOp",EDGE,"E116.MirrorCS")])],"isStart":false});
            var Q1;
            Q1=makeQuery(id+"F16.opExtrude","CAP_EDGE",EDGE,{"disambiguationData":[OSD([sQuery(id+"F15.wireOp",EDGE,"E105.right")])],"isStart":false});
            chamfer(context, id + "F23", {"entities" : qUnion([Q0, Q1]), "chamferType" : ChamferType.TWO_OFFSETS, "width1" : .5 * mm, "oppositeDirection" : false, "width2" : 3 * mm, "tangentPropagation" : true});
        }
        {
            var Q0;
            Q0=makeQuery(id+"F16.opExtrude","CAP_EDGE",EDGE,{"disambiguationData":[OSD([sQuery(id+"F15.wireOp",EDGE,"E114.MirrorCS")])],"isStart":false});
            var Q1;
            Q1=makeQuery(id+"F16.opExtrude","CAP_EDGE",EDGE,{"disambiguationData":[OSD([sQuery(id+"F15.wireOp",EDGE,"E107.MirrorCS")])],"isStart":false});
            chamfer(context, id + "F24", {"entities" : qUnion([Q0, Q1]), "chamferType" : ChamferType.TWO_OFFSETS, "width1" : 3 * mm, "oppositeDirection" : false, "width2" : .5 * mm, "tangentPropagation" : true});
        }
        {
            var Q0;
            {var subQ0=sQuery(id+"F6.wireOp",EDGE,"E29.3");var subQ1=sQuery(id+"F6.wireOp",EDGE,"E29.1");var subQ2=sQuery(id+"F6.wireOp",EDGE,"E28.0");var subQ3=sQuery(id+"F6.wireOp",EDGE,"E25.0");Q0=makeQuery(id+"F13.boolean.opBoolean","MERGE",FACE,{"derivedFrom":[makeQuery(id+"F11.boolean.opBoolean","MERGE",FACE,{"derivedFrom":[makeQuery(id+"F3.opExtrude","CAP_FACE",FACE,{"disambiguationData":[OSD([sQuery(id+"F2.wireOp",EDGE,"E16.0"),sQuery(id+"F2.wireOp",EDGE,"E17.0"),sQuery(id+"F2.wireOp",EDGE,"E18.0"),sQuery(id+"F2.wireOp",EDGE,"E19.0"),sQuery(id+"F2.wireOp",EDGE,"E20.0"),sQuery(id+"F2.wireOp",EDGE,"E21.0"),sQuery(id+"F2.wireOp",EDGE,"E22.0"),sQuery(id+"F2.wireOp",EDGE,"E23.0"),sQuery(id+"F2.wireOp",EDGE,"E24.0"),sQuery(id+"F2.wireOp",EDGE,"E24.1"),sQuery(id+"F2.wireOp",EDGE,"E24.2"),sQuery(id+"F2.wireOp",EDGE,"E24.3"),sQuery(id+"F2.wireOp",EDGE,"E24.4"),sQuery(id+"F2.wireOp",EDGE,"E24.5"),sQuery(id+"F2.wireOp",EDGE,"E24.6"),sQuery(id+"F2.wireOp",EDGE,"E24.7")])],"isStart":false}),makeQuery(id+"F7.opExtrude","CAP_FACE",FACE,{"disambiguationData":[OSD([subQ3,sQuery(id+"F6.wireOp",EDGE,"E27.0"),subQ2,subQ1,sQuery(id+"F6.wireOp",EDGE,"E29.2"),subQ0,sQuery(id+"F6.wireOp",EDGE,"E31"),sQuery(id+"F6.wireOp",EDGE,"E39.MirrorCS")])],"isStart":false}),makeQuery(id+"F7.opExtrude","CAP_FACE",FACE,{"disambiguationData":[OSD([subQ3,sQuery(id+"F6.wireOp",EDGE,"E26.0"),subQ2,sQuery(id+"F6.wireOp",EDGE,"E29.0"),subQ1,subQ0,sQuery(id+"F6.wireOp",EDGE,"E35.MirrorCS"),sQuery(id+"F6.wireOp",EDGE,"E36.MirrorCS")])],"isStart":false}),makeQuery(id+"F11.opExtrude","CAP_FACE",FACE,{"disambiguationData":[OSD([sQuery(id+"F10.wireOp",EDGE,"E44.bottom"),sQuery(id+"F10.wireOp",EDGE,"E44.top"),sQuery(id+"F10.wireOp",EDGE,"E44.left"),sQuery(id+"F10.wireOp",EDGE,"E44.right")])],"isStart":true}),makeQuery(id+"F11.opExtrude","CAP_FACE",FACE,{"disambiguationData":[OSD([sQuery(id+"F10.wireOp",EDGE,"E45.bottom"),sQuery(id+"F10.wireOp",EDGE,"E45.top"),sQuery(id+"F10.wireOp",EDGE,"E45.left"),sQuery(id+"F10.wireOp",EDGE,"E45.right")])],"isStart":true}),makeQuery(id+"F11.opExtrude","CAP_FACE",FACE,{"disambiguationData":[OSD([sQuery(id+"F10.wireOp",EDGE,"E46.bottom"),sQuery(id+"F10.wireOp",EDGE,"E46.top"),sQuery(id+"F10.wireOp",EDGE,"E46.left"),sQuery(id+"F10.wireOp",EDGE,"E46.right")])],"isStart":true}),makeQuery(id+"F11.opExtrude","CAP_FACE",FACE,{"disambiguationData":[OSD([sQuery(id+"F10.wireOp",EDGE,"E47.MirrorCS"),sQuery(id+"F10.wireOp",EDGE,"E49.MirrorCS"),sQuery(id+"F10.wireOp",EDGE,"E53.MirrorCS"),sQuery(id+"F10.wireOp",EDGE,"E58.MirrorCS")])],"isStart":true}),makeQuery(id+"F11.opExtrude","CAP_FACE",FACE,{"disambiguationData":[OSD([sQuery(id+"F10.wireOp",EDGE,"E48.MirrorCS"),sQuery(id+"F10.wireOp",EDGE,"E50.MirrorCS"),sQuery(id+"F10.wireOp",EDGE,"E56.MirrorCS"),sQuery(id+"F10.wireOp",EDGE,"E59.MirrorCS")])],"isStart":true}),makeQuery(id+"F11.opExtrude","CAP_FACE",FACE,{"disambiguationData":[OSD([sQuery(id+"F10.wireOp",EDGE,"E51.MirrorCS"),sQuery(id+"F10.wireOp",EDGE,"E52.MirrorCS"),sQuery(id+"F10.wireOp",EDGE,"E54.MirrorCS"),sQuery(id+"F10.wireOp",EDGE,"E57.MirrorCS")])],"isStart":true}),makeQuery(id+"F11.opExtrude","CAP_FACE",FACE,{"disambiguationData":[OSD([sQuery(id+"F10.wireOp",EDGE,"E60.MirrorCS"),sQuery(id+"F10.wireOp",EDGE,"E68.MirrorCS"),sQuery(id+"F10.wireOp",EDGE,"E73.MirrorCS"),sQuery(id+"F10.wireOp",EDGE,"E74.MirrorCS")])],"isStart":true}),makeQuery(id+"F11.opExtrude","CAP_FACE",FACE,{"disambiguationData":[OSD([sQuery(id+"F10.wireOp",EDGE,"E61.MirrorCS"),sQuery(id+"F10.wireOp",EDGE,"E66.MirrorCS"),sQuery(id+"F10.wireOp",EDGE,"E72.MirrorCS"),sQuery(id+"F10.wireOp",EDGE,"E85.MirrorCS")])],"isStart":true}),makeQuery(id+"F11.opExtrude","CAP_FACE",FACE,{"disambiguationData":[OSD([sQuery(id+"F10.wireOp",EDGE,"E62.MirrorCS"),sQuery(id+"F10.wireOp",EDGE,"E64.MirrorCS"),sQuery(id+"F10.wireOp",EDGE,"E79.MirrorCS"),sQuery(id+"F10.wireOp",EDGE,"E82.MirrorCS")])],"isStart":true}),makeQuery(id+"F11.opExtrude","CAP_FACE",FACE,{"disambiguationData":[OSD([sQuery(id+"F10.wireOp",EDGE,"E63.MirrorCS"),sQuery(id+"F10.wireOp",EDGE,"E65.MirrorCS"),sQuery(id+"F10.wireOp",EDGE,"E80.MirrorCS"),sQuery(id+"F10.wireOp",EDGE,"E81.MirrorCS")])],"isStart":true}),makeQuery(id+"F11.opExtrude","CAP_FACE",FACE,{"disambiguationData":[OSD([sQuery(id+"F10.wireOp",EDGE,"E67.MirrorCS"),sQuery(id+"F10.wireOp",EDGE,"E70.MirrorCS"),sQuery(id+"F10.wireOp",EDGE,"E76.MirrorCS"),sQuery(id+"F10.wireOp",EDGE,"E83.MirrorCS")])],"isStart":true}),makeQuery(id+"F11.opExtrude","CAP_FACE",FACE,{"disambiguationData":[OSD([sQuery(id+"F10.wireOp",EDGE,"E69.MirrorCS"),sQuery(id+"F10.wireOp",EDGE,"E71.MirrorCS"),sQuery(id+"F10.wireOp",EDGE,"E77.MirrorCS"),sQuery(id+"F10.wireOp",EDGE,"E84.MirrorCS")])],"isStart":true})]}),makeQuery(id+"F13.opExtrude","CAP_FACE",FACE,{"disambiguationData":[OSD([sQuery(id+"F12.wireOp",EDGE,"E88.bottom"),sQuery(id+"F12.wireOp",EDGE,"E88.top"),sQuery(id+"F12.wireOp",EDGE,"E88.left"),sQuery(id+"F12.wireOp",EDGE,"E88.right")])],"isStart":true}),makeQuery(id+"F13.opExtrude","CAP_FACE",FACE,{"disambiguationData":[OSD([sQuery(id+"F12.wireOp",EDGE,"E89.MirrorCS"),sQuery(id+"F12.wireOp",EDGE,"E90.MirrorCS"),sQuery(id+"F12.wireOp",EDGE,"E91.MirrorCS"),sQuery(id+"F12.wireOp",EDGE,"E92.MirrorCS")])],"isStart":true}),makeQuery(id+"F13.opExtrude","CAP_FACE",FACE,{"disambiguationData":[OSD([sQuery(id+"F12.wireOp",EDGE,"E93.MirrorCS"),sQuery(id+"F12.wireOp",EDGE,"E95.MirrorCS"),sQuery(id+"F12.wireOp",EDGE,"E98.MirrorCS"),sQuery(id+"F12.wireOp",EDGE,"E99.MirrorCS")])],"isStart":true}),makeQuery(id+"F13.opExtrude","CAP_FACE",FACE,{"disambiguationData":[OSD([sQuery(id+"F12.wireOp",EDGE,"E94.MirrorCS"),sQuery(id+"F12.wireOp",EDGE,"E96.MirrorCS"),sQuery(id+"F12.wireOp",EDGE,"E97.MirrorCS"),sQuery(id+"F12.wireOp",EDGE,"E100.MirrorCS")])],"isStart":true})]});}
            var sketch = newSketch(context, id + "F25", { "sketchPlane" : qUnion([Q0])});
            skLineSegment(sketch, "E136.0", {"start": v(-93, -56.25) * mm, "end": v(-93, 56.25) * mm, "construction": true});
            skLineSegment(sketch, "E137.0", {"start": v(-89.1, -30.25) * mm, "end": v(-89.1, -38.95) * mm, "construction": true});
            skLineSegment(sketch, "E138.0", {"start": v(-87.5, -49.75) * mm, "end": v(-87.5, 49.75) * mm, "construction": true});
            skPoint(sketch, "E139.0", {"position": v(-87.5, -27.45) * mm});
            skLineSegment(sketch, "E140.bottom", {"start": v(-89.1, -38.95) * mm, "end": v(-93, -38.95) * mm});
            skLineSegment(sketch, "E140.top", {"start": v(-89.1, -38.15) * mm, "end": v(-93, -38.15) * mm});
            skLineSegment(sketch, "E140.left", {"start": v(-89.1, -38.95) * mm, "end": v(-89.1, -38.15) * mm});
            skLineSegment(sketch, "E140.right", {"start": v(-93, -38.95) * mm, "end": v(-93, -38.15) * mm});
            skLineSegment(sketch, "E141.bottom", {"start": v(-89.1, -30.25) * mm, "end": v(-93, -30.25) * mm});
            skLineSegment(sketch, "E141.top", {"start": v(-89.1, -31.05) * mm, "end": v(-93, -31.05) * mm});
            skLineSegment(sketch, "E141.left", {"start": v(-89.1, -30.25) * mm, "end": v(-89.1, -31.05) * mm});
            skLineSegment(sketch, "E141.right", {"start": v(-93, -30.25) * mm, "end": v(-93, -31.05) * mm});
            skLineSegment(sketch, "E142.bottom", {"start": v(-87.5, -24.25) * mm, "end": v(-93, -24.25) * mm});
            skLineSegment(sketch, "E142.top", {"start": v(-87.5, -25.05) * mm, "end": v(-93, -25.05) * mm});
            skLineSegment(sketch, "E142.left", {"start": v(-87.5, -24.25) * mm, "end": v(-87.5, -25.05) * mm});
            skLineSegment(sketch, "E142.right", {"start": v(-93, -24.25) * mm, "end": v(-93, -25.05) * mm});
            skLineSegment(sketch, "E143.MirrorCS", {"start": v(-89.1, 38.95) * mm, "end": v(-89.1, 38.15) * mm});
            skLineSegment(sketch, "E144.MirrorCS", {"start": v(-89.1, 38.95) * mm, "end": v(-93, 38.95) * mm});
            skLineSegment(sketch, "E145.MirrorCS", {"start": v(-93, 38.95) * mm, "end": v(-93, 38.15) * mm});
            skLineSegment(sketch, "E146.MirrorCS", {"start": v(-89.1, 38.15) * mm, "end": v(-93, 38.15) * mm});
            skLineSegment(sketch, "E147.MirrorCS", {"start": v(-89.1, 30.25) * mm, "end": v(-89.1, 31.05) * mm});
            skLineSegment(sketch, "E148.MirrorCS", {"start": v(-89.1, 30.25) * mm, "end": v(-93, 30.25) * mm});
            skLineSegment(sketch, "E149.MirrorCS", {"start": v(-89.1, 31.05) * mm, "end": v(-93, 31.05) * mm});
            skLineSegment(sketch, "E150.MirrorCS", {"start": v(-93, 30.25) * mm, "end": v(-93, 31.05) * mm});
            skLineSegment(sketch, "E151.MirrorCS", {"start": v(-87.5, 24.25) * mm, "end": v(-93, 24.25) * mm});
            skLineSegment(sketch, "E152.MirrorCS", {"start": v(-93, 24.25) * mm, "end": v(-93, 25.05) * mm});
            skLineSegment(sketch, "E153.MirrorCS", {"start": v(-87.5, 25.05) * mm, "end": v(-93, 25.05) * mm});
            skLineSegment(sketch, "E154.MirrorCS", {"start": v(-87.5, 24.25) * mm, "end": v(-87.5, 25.05) * mm});
            skLineSegment(sketch, "E155.MirrorCS", {"start": v(93, 30.25) * mm, "end": v(93, 31.05) * mm});
            skLineSegment(sketch, "E156.MirrorCS", {"start": v(89.1, 38.95) * mm, "end": v(89.1, 38.15) * mm});
            skLineSegment(sketch, "E157.MirrorCS", {"start": v(87.5, 24.25) * mm, "end": v(87.5, 25.05) * mm});
            skLineSegment(sketch, "E158.MirrorCS", {"start": v(93, 24.25) * mm, "end": v(93, 25.05) * mm});
            skLineSegment(sketch, "E159.MirrorCS", {"start": v(93, 38.95) * mm, "end": v(93, 38.15) * mm});
            skLineSegment(sketch, "E160.MirrorCS", {"start": v(89.1, 30.25) * mm, "end": v(89.1, 31.05) * mm});
            skLineSegment(sketch, "E161.MirrorCS", {"start": v(89.1, 38.15) * mm, "end": v(93, 38.15) * mm});
            skLineSegment(sketch, "E162.MirrorCS", {"start": v(89.1, 38.95) * mm, "end": v(93, 38.95) * mm});
            skLineSegment(sketch, "E163.MirrorCS", {"start": v(89.1, 30.25) * mm, "end": v(93, 30.25) * mm});
            skLineSegment(sketch, "E164.MirrorCS", {"start": v(89.1, 31.05) * mm, "end": v(93, 31.05) * mm});
            skLineSegment(sketch, "E165.MirrorCS", {"start": v(87.5, 25.05) * mm, "end": v(93, 25.05) * mm});
            skLineSegment(sketch, "E166.MirrorCS", {"start": v(87.5, 24.25) * mm, "end": v(93, 24.25) * mm});
            skLineSegment(sketch, "E167.MirrorCS", {"start": v(87.5, -24.25) * mm, "end": v(87.5, -25.05) * mm});
            skLineSegment(sketch, "E168.MirrorCS", {"start": v(87.5, -24.25) * mm, "end": v(93, -24.25) * mm});
            skLineSegment(sketch, "E169.MirrorCS", {"start": v(93, -24.25) * mm, "end": v(93, -25.05) * mm});
            skLineSegment(sketch, "E170.MirrorCS", {"start": v(87.5, -25.05) * mm, "end": v(93, -25.05) * mm});
            skLineSegment(sketch, "E171.MirrorCS", {"start": v(89.1, -30.25) * mm, "end": v(93, -30.25) * mm});
            skLineSegment(sketch, "E172.MirrorCS", {"start": v(89.1, -31.05) * mm, "end": v(93, -31.05) * mm});
            skLineSegment(sketch, "E173.MirrorCS", {"start": v(93, -30.25) * mm, "end": v(93, -31.05) * mm});
            skLineSegment(sketch, "E174.MirrorCS", {"start": v(89.1, -30.25) * mm, "end": v(89.1, -31.05) * mm});
            skLineSegment(sketch, "E175.MirrorCS", {"start": v(93, -38.95) * mm, "end": v(93, -38.15) * mm});
            skLineSegment(sketch, "E176.MirrorCS", {"start": v(89.1, -38.95) * mm, "end": v(89.1, -38.15) * mm});
            skLineSegment(sketch, "E177.MirrorCS", {"start": v(89.1, -38.95) * mm, "end": v(93, -38.95) * mm});
            skLineSegment(sketch, "E178.MirrorCS", {"start": v(89.1, -38.15) * mm, "end": v(93, -38.15) * mm});
            skSolve(sketch);
        }
        {
            var Q0;
            Q0 = qSketchRegion(id + "F25", true);
            extrude(context, id + "F26", {"entities" : qUnion([Q0]), "operationType" : NewBodyOperationType.ADD, "endBound" : BoundingType.UP_TO_NEXT, "oppositeDirection" : true, "depth" : 25 * mm, "offsetDistance" : 25 * mm});
        }
    });
